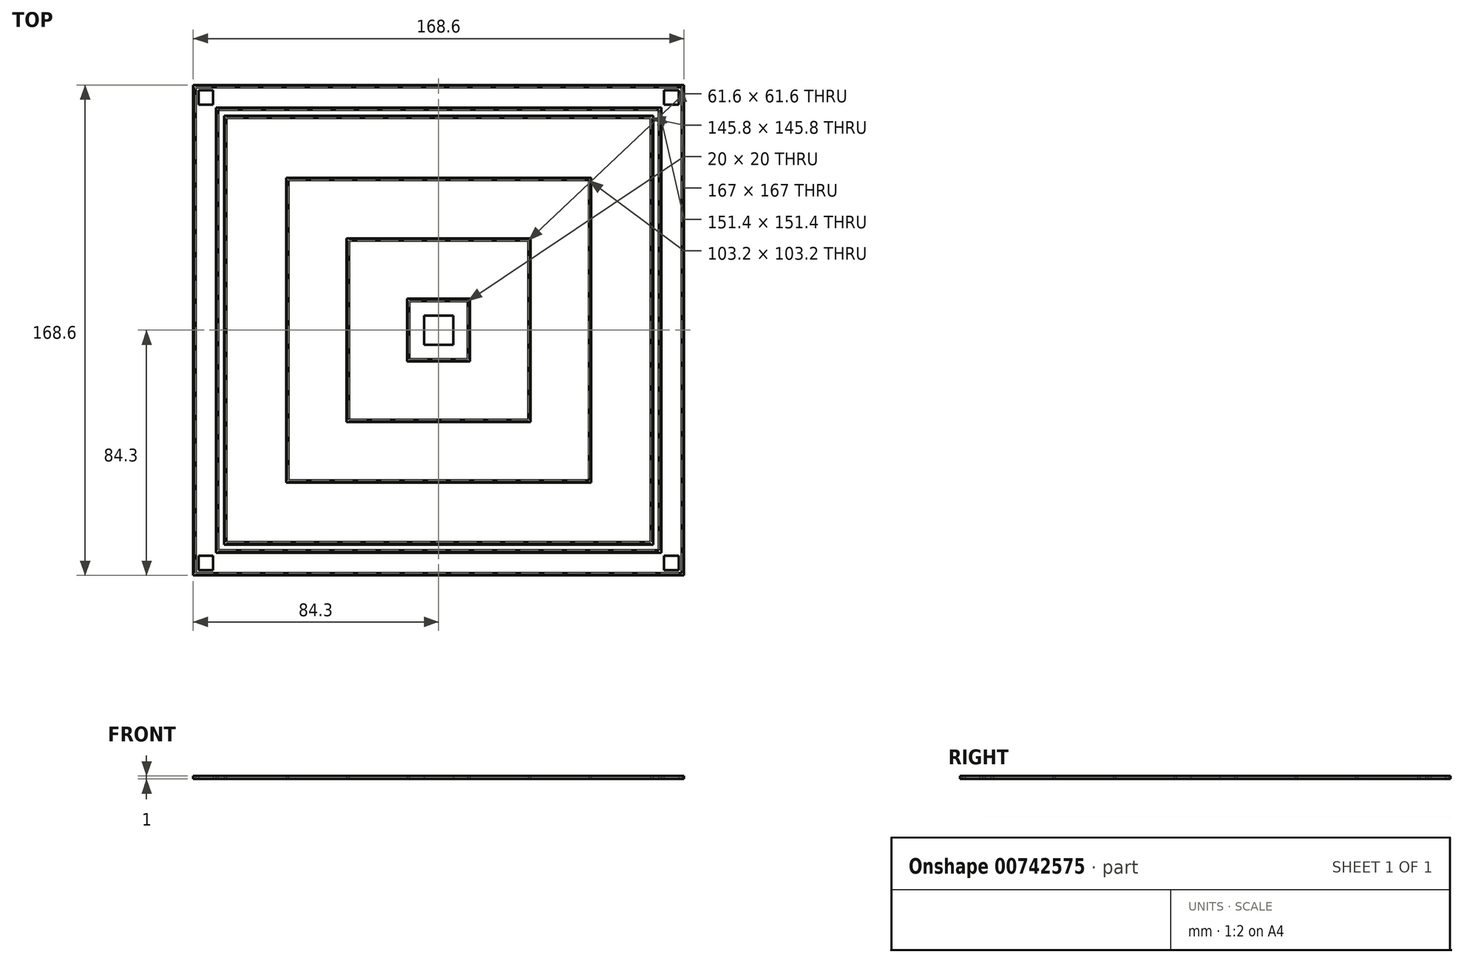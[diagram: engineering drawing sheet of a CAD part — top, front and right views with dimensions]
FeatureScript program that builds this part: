
annotation { "Feature Type Name" : "Feature", "Feature Type Description" : "" }
export const myFeature = defineFeature(function(context is Context, id is Id, definition is map)
    precondition{}
    {
        {
            var Q0;
            Q0=qCreatedBy(makeId("Top.planeOp"),FACE);
            var sketch = newSketch(context, id + "F0", { "sketchPlane" : qUnion([Q0])});
            skLineSegment(sketch, "E0.bottom", {"start": v(-80, 80) * mm, "end": v(80, 80) * mm, "construction": true});
            skLineSegment(sketch, "E0.top", {"start": v(-80, -80) * mm, "end": v(80, -80) * mm, "construction": true});
            skLineSegment(sketch, "E0.left", {"start": v(-80, 80) * mm, "end": v(-80, -80) * mm, "construction": true});
            skLineSegment(sketch, "E0.right", {"start": v(80, 80) * mm, "end": v(80, -80) * mm, "construction": true});
            skPoint(sketch, "E0.middle", {"position": v(0, 0) * mm});
            skLineSegment(sketch, "E1.bottom", {"start": v(-82.5, 82.5) * mm, "end": v(-77.5, 82.5) * mm});
            skLineSegment(sketch, "E1.top", {"start": v(-82.5, 77.5) * mm, "end": v(-77.5, 77.5) * mm});
            skLineSegment(sketch, "E1.left", {"start": v(-82.5, 82.5) * mm, "end": v(-82.5, 77.5) * mm});
            skLineSegment(sketch, "E1.right", {"start": v(-77.5, 82.5) * mm, "end": v(-77.5, 77.5) * mm});
            skPoint(sketch, "E1.middle", {"position": v(-80, 80) * mm});
            skLineSegment(sketch, "E2.bottom", {"start": v(-82.5, -77.5) * mm, "end": v(-77.5, -77.5) * mm});
            skLineSegment(sketch, "E2.top", {"start": v(-82.5, -82.5) * mm, "end": v(-77.5, -82.5) * mm});
            skLineSegment(sketch, "E2.left", {"start": v(-82.5, -77.5) * mm, "end": v(-82.5, -82.5) * mm});
            skLineSegment(sketch, "E2.right", {"start": v(-77.5, -77.5) * mm, "end": v(-77.5, -82.5) * mm});
            skPoint(sketch, "E2.middle", {"position": v(-80, -80) * mm});
            skLineSegment(sketch, "E3.bottom", {"start": v(77.5, -77.5) * mm, "end": v(82.5, -77.5) * mm});
            skLineSegment(sketch, "E3.top", {"start": v(77.5, -82.5) * mm, "end": v(82.5, -82.5) * mm});
            skLineSegment(sketch, "E3.left", {"start": v(77.5, -77.5) * mm, "end": v(77.5, -82.5) * mm});
            skLineSegment(sketch, "E3.right", {"start": v(82.5, -77.5) * mm, "end": v(82.5, -82.5) * mm});
            skPoint(sketch, "E3.middle", {"position": v(80, -80) * mm});
            skLineSegment(sketch, "E4.bottom", {"start": v(77.5, 77.5) * mm, "end": v(82.5, 77.5) * mm});
            skLineSegment(sketch, "E4.top", {"start": v(77.5, 82.5) * mm, "end": v(82.5, 82.5) * mm});
            skLineSegment(sketch, "E4.left", {"start": v(77.5, 77.5) * mm, "end": v(77.5, 82.5) * mm});
            skLineSegment(sketch, "E4.right", {"start": v(82.5, 77.5) * mm, "end": v(82.5, 82.5) * mm});
            skPoint(sketch, "E4.middle", {"position": v(80, 80) * mm});
            skLineSegment(sketch, "E5.bottom", {"start": v(-5, 5) * mm, "end": v(5, 5) * mm});
            skLineSegment(sketch, "E5.top", {"start": v(-5, -5) * mm, "end": v(5, -5) * mm});
            skLineSegment(sketch, "E5.left", {"start": v(-5, 5) * mm, "end": v(-5, -5) * mm});
            skLineSegment(sketch, "E5.right", {"start": v(5, 5) * mm, "end": v(5, -5) * mm});
            skLineSegment(sketch, "E6.bottom", {"start": v(-76.5, 76.5) * mm, "end": v(76.5, 76.5) * mm});
            skLineSegment(sketch, "E6.top", {"start": v(-76.5, -76.5) * mm, "end": v(76.5, -76.5) * mm});
            skLineSegment(sketch, "E6.left", {"start": v(-76.5, 76.5) * mm, "end": v(-76.5, -76.5) * mm});
            skLineSegment(sketch, "E6.right", {"start": v(76.5, 76.5) * mm, "end": v(76.5, -76.5) * mm});
            skLineSegment(sketch, "E7.bottom", {"start": v(-75.7, 75.7) * mm, "end": v(75.7, 75.7) * mm});
            skLineSegment(sketch, "E7.top", {"start": v(-75.7, -75.7) * mm, "end": v(75.7, -75.7) * mm});
            skLineSegment(sketch, "E7.left", {"start": v(-75.7, 75.7) * mm, "end": v(-75.7, -75.7) * mm});
            skLineSegment(sketch, "E7.right", {"start": v(75.7, 75.7) * mm, "end": v(75.7, -75.7) * mm});
            skLineSegment(sketch, "E8.bottom", {"start": v(-73.7, 73.7) * mm, "end": v(73.7, 73.7) * mm});
            skLineSegment(sketch, "E8.top", {"start": v(-73.7, -73.7) * mm, "end": v(73.7, -73.7) * mm});
            skLineSegment(sketch, "E8.left", {"start": v(-73.7, 73.7) * mm, "end": v(-73.7, -73.7) * mm});
            skLineSegment(sketch, "E8.right", {"start": v(73.7, 73.7) * mm, "end": v(73.7, -73.7) * mm});
            skLineSegment(sketch, "E9.bottom", {"start": v(-72.9, 72.9) * mm, "end": v(72.9, 72.9) * mm});
            skLineSegment(sketch, "E9.top", {"start": v(-72.9, -72.9) * mm, "end": v(72.9, -72.9) * mm});
            skLineSegment(sketch, "E9.left", {"start": v(-72.9, 72.9) * mm, "end": v(-72.9, -72.9) * mm});
            skLineSegment(sketch, "E9.right", {"start": v(72.9, 72.9) * mm, "end": v(72.9, -72.9) * mm});
            skLineSegment(sketch, "E10.bottom", {"start": v(-83.5, 83.5) * mm, "end": v(83.5, 83.5) * mm});
            skLineSegment(sketch, "E10.top", {"start": v(-83.5, -83.5) * mm, "end": v(83.5, -83.5) * mm});
            skLineSegment(sketch, "E10.left", {"start": v(-83.5, 83.5) * mm, "end": v(-83.5, -83.5) * mm});
            skLineSegment(sketch, "E10.right", {"start": v(83.5, 83.5) * mm, "end": v(83.5, -83.5) * mm});
            skLineSegment(sketch, "E11.bottom", {"start": v(-84.3, 84.3) * mm, "end": v(84.3, 84.3) * mm});
            skLineSegment(sketch, "E11.top", {"start": v(-84.3, -84.3) * mm, "end": v(84.3, -84.3) * mm});
            skLineSegment(sketch, "E11.left", {"start": v(-84.3, 84.3) * mm, "end": v(-84.3, -84.3) * mm});
            skLineSegment(sketch, "E11.right", {"start": v(84.3, 84.3) * mm, "end": v(84.3, -84.3) * mm});
            skLineSegment(sketch, "E12.bottom", {"start": v(-52.4, 52.4) * mm, "end": v(52.4, 52.4) * mm});
            skLineSegment(sketch, "E12.top", {"start": v(-52.4, -52.4) * mm, "end": v(52.4, -52.4) * mm});
            skLineSegment(sketch, "E12.left", {"start": v(-52.4, 52.4) * mm, "end": v(-52.4, -52.4) * mm});
            skLineSegment(sketch, "E12.right", {"start": v(52.4, 52.4) * mm, "end": v(52.4, -52.4) * mm});
            skLineSegment(sketch, "E13.bottom", {"start": v(-51.6, 51.6) * mm, "end": v(51.6, 51.6) * mm});
            skLineSegment(sketch, "E13.top", {"start": v(-51.6, -51.6) * mm, "end": v(51.6, -51.6) * mm});
            skLineSegment(sketch, "E13.left", {"start": v(-51.6, 51.6) * mm, "end": v(-51.6, -51.6) * mm});
            skLineSegment(sketch, "E13.right", {"start": v(51.6, 51.6) * mm, "end": v(51.6, -51.6) * mm});
            skLineSegment(sketch, "E14.bottom", {"start": v(-31.6, 31.6) * mm, "end": v(31.6, 31.6) * mm});
            skLineSegment(sketch, "E14.top", {"start": v(-31.6, -31.6) * mm, "end": v(31.6, -31.6) * mm});
            skLineSegment(sketch, "E14.left", {"start": v(-31.6, 31.6) * mm, "end": v(-31.6, -31.6) * mm});
            skLineSegment(sketch, "E14.right", {"start": v(31.6, 31.6) * mm, "end": v(31.6, -31.6) * mm});
            skLineSegment(sketch, "E15.bottom", {"start": v(-30.8, 30.8) * mm, "end": v(30.8, 30.8) * mm});
            skLineSegment(sketch, "E15.top", {"start": v(-30.8, -30.8) * mm, "end": v(30.8, -30.8) * mm});
            skLineSegment(sketch, "E15.left", {"start": v(-30.8, 30.8) * mm, "end": v(-30.8, -30.8) * mm});
            skLineSegment(sketch, "E15.right", {"start": v(30.8, 30.8) * mm, "end": v(30.8, -30.8) * mm});
            skLineSegment(sketch, "E16.bottom", {"start": v(-10.8, 10.8) * mm, "end": v(10.8, 10.8) * mm});
            skLineSegment(sketch, "E16.top", {"start": v(-10.8, -10.8) * mm, "end": v(10.8, -10.8) * mm});
            skLineSegment(sketch, "E16.left", {"start": v(-10.8, 10.8) * mm, "end": v(-10.8, -10.8) * mm});
            skLineSegment(sketch, "E16.right", {"start": v(10.8, 10.8) * mm, "end": v(10.8, -10.8) * mm});
            skLineSegment(sketch, "E17.bottom", {"start": v(-10, 10) * mm, "end": v(10, 10) * mm});
            skLineSegment(sketch, "E17.top", {"start": v(-10, -10) * mm, "end": v(10, -10) * mm});
            skLineSegment(sketch, "E17.left", {"start": v(-10, 10) * mm, "end": v(-10, -10) * mm});
            skLineSegment(sketch, "E17.right", {"start": v(10, 10) * mm, "end": v(10, -10) * mm});
            skLineSegment(sketch, "E18.top", {"start": v(-80, -80) * mm, "end": v(80, -80) * mm});
            skSolve(sketch);
        }
        {
            var Q0;
            Q0=makeQuery(id+"F0.imprint","IMPRINT",FACE,{"disambiguationData":[TD([[makeQuery(id+"F0.imprint","IMPRINT",EDGE,{"derivedFrom":sQuery(id+"F0.wireOp",EDGE,"E10.bottom")}),1.0]])]});
            var Q1;
            {var subQ1=sQuery(id+"F0.wireOp",EDGE,"E1.bottom");Q1=makeQuery(id+"F0.imprint","IMPRINT",FACE,{"disambiguationData":[TD([[makeQuery(id+"F0.imprint","IMPRINT",EDGE,{"derivedFrom":subQ1}),-1.0]])]});}
            var Q2;
            {var subQ3=sQuery(id+"F0.wireOp",EDGE,"E18.left");var subQ5=sQuery(id+"F0.wireOp",EDGE,"E18.bottom");var subQ7=makeQuery(id+"F0.imprint","INTERSECT",VERTEX,{"derivedFrom":[subQ5,subQ3]});Q2=makeQuery(id+"F0.imprint","IMPRINT",FACE,{"disambiguationData":[TD([[makeQuery(id+"F0.imprint","IMPRINT",EDGE,{"disambiguationData":[TD([[subQ7,-1.0]])],"derivedFrom":subQ5}),-1.0]])]});}
            var Q3;
            {var subQ0=sQuery(id+"F0.wireOp",EDGE,"qftvMAqE-KtSR-YpLS-TIVa-jHuJledwcVvA.left");Q3=makeQuery(id+"F0.imprint","IMPRINT",FACE,{"disambiguationData":[TD([[makeQuery(id+"F0.imprint","IMPRINT",EDGE,{"derivedFrom":subQ0}),-1.0]])]});}
            var Q4;
            {var subQ0=sQuery(id+"F0.wireOp",EDGE,"qftvMAqE-KtSR-YpLS-TIVa-jHuJledwcVvA.bottom");Q4=makeQuery(id+"F0.imprint","IMPRINT",FACE,{"disambiguationData":[TD([[makeQuery(id+"F0.imprint","IMPRINT",EDGE,{"derivedFrom":subQ0}),1.0]])]});}
            var Q5;
            Q5=makeQuery(id+"F0.imprint","IMPRINT",FACE,{"disambiguationData":[TD([[makeQuery(id+"F0.imprint","IMPRINT",EDGE,{"derivedFrom":sQuery(id+"F0.wireOp",EDGE,"E6.bottom")}),-1.0]])]});
            var Q6;
            Q6=makeQuery(id+"F0.imprint","IMPRINT",FACE,{"disambiguationData":[TD([[makeQuery(id+"F0.imprint","IMPRINT",EDGE,{"derivedFrom":sQuery(id+"F0.wireOp",EDGE,"E8.bottom")}),-1.0]])]});
            var Q7;
            Q7=makeQuery(id+"F0.imprint","IMPRINT",FACE,{"disambiguationData":[TD([[makeQuery(id+"F0.imprint","IMPRINT",EDGE,{"derivedFrom":sQuery(id+"F0.wireOp",EDGE,"E12.bottom")}),-1.0]])]});
            var Q8;
            Q8=makeQuery(id+"F0.imprint","IMPRINT",FACE,{"disambiguationData":[TD([[makeQuery(id+"F0.imprint","IMPRINT",EDGE,{"derivedFrom":sQuery(id+"F0.wireOp",EDGE,"E14.bottom")}),-1.0]])]});
            var Q9;
            Q9=makeQuery(id+"F0.imprint","IMPRINT",FACE,{"disambiguationData":[TD([[makeQuery(id+"F0.imprint","IMPRINT",EDGE,{"derivedFrom":sQuery(id+"F0.wireOp",EDGE,"E16.bottom")}),-1.0]])]});
            var Q10;
            Q10=makeQuery(id+"F0.imprint","IMPRINT",FACE,{"disambiguationData":[TD([[makeQuery(id+"F0.imprint","IMPRINT",EDGE,{"derivedFrom":sQuery(id+"F0.wireOp",EDGE,"E5.bottom")}),-1.0]])]});
            var Q11;
            {var subQ3=sQuery(id+"F0.wireOp",EDGE,"E18.right");var subQ5=sQuery(id+"F0.wireOp",EDGE,"E18.bottom");var subQ7=makeQuery(id+"F0.imprint","INTERSECT",VERTEX,{"derivedFrom":[subQ5,subQ3]});Q11=makeQuery(id+"F0.imprint","IMPRINT",FACE,{"disambiguationData":[TD([[makeQuery(id+"F0.imprint","IMPRINT",EDGE,{"disambiguationData":[TD([[subQ7,1.0]])],"derivedFrom":subQ5}),-1.0]])]});}
            var Q12;
            {var subQ7=sQuery(id+"F0.wireOp",EDGE,"E4.top");Q12=makeQuery(id+"F0.imprint","IMPRINT",FACE,{"disambiguationData":[TD([[makeQuery(id+"F0.imprint","IMPRINT",EDGE,{"derivedFrom":subQ7}),-1.0]])]});}
            var Q13;
            {var subQ0=sQuery(id+"F0.wireOp",EDGE,"qftvMAqE-KtSR-YpLS-TIVa-jHuJledwcVvA.right");Q13=makeQuery(id+"F0.imprint","IMPRINT",FACE,{"disambiguationData":[TD([[makeQuery(id+"F0.imprint","IMPRINT",EDGE,{"derivedFrom":subQ0}),1.0]])]});}
            var Q14;
            {var subQ2=sQuery(id+"F0.wireOp",EDGE,"E3.top");Q14=makeQuery(id+"F0.imprint","IMPRINT",FACE,{"disambiguationData":[TD([[makeQuery(id+"F0.imprint","IMPRINT",EDGE,{"derivedFrom":subQ2}),1.0]])]});}
            var Q15;
            {var subQ3=sQuery(id+"F0.wireOp",EDGE,"E18.right");var subQ5=sQuery(id+"F0.wireOp",EDGE,"E18.top");var subQ7=makeQuery(id+"F0.imprint","INTERSECT",VERTEX,{"derivedFrom":[subQ5,subQ3]});Q15=makeQuery(id+"F0.imprint","IMPRINT",FACE,{"disambiguationData":[TD([[makeQuery(id+"F0.imprint","IMPRINT",EDGE,{"disambiguationData":[TD([[subQ7,1.0]])],"derivedFrom":subQ5}),1.0]])]});}
            var Q16;
            {var subQ0=sQuery(id+"F0.wireOp",EDGE,"qftvMAqE-KtSR-YpLS-TIVa-jHuJledwcVvA.top");Q16=makeQuery(id+"F0.imprint","IMPRINT",FACE,{"disambiguationData":[TD([[makeQuery(id+"F0.imprint","IMPRINT",EDGE,{"derivedFrom":subQ0}),-1.0]])]});}
            var Q17;
            {var subQ1=sQuery(id+"F0.wireOp",EDGE,"E2.top");Q17=makeQuery(id+"F0.imprint","IMPRINT",FACE,{"disambiguationData":[TD([[makeQuery(id+"F0.imprint","IMPRINT",EDGE,{"derivedFrom":subQ1}),1.0]])]});}
            var Q18;
            {var subQ3=sQuery(id+"F0.wireOp",EDGE,"E18.left");var subQ5=sQuery(id+"F0.wireOp",EDGE,"E18.top");var subQ7=makeQuery(id+"F0.imprint","INTERSECT",VERTEX,{"derivedFrom":[subQ5,subQ3]});Q18=makeQuery(id+"F0.imprint","IMPRINT",FACE,{"disambiguationData":[TD([[makeQuery(id+"F0.imprint","IMPRINT",EDGE,{"disambiguationData":[TD([[subQ7,-1.0]])],"derivedFrom":subQ5}),1.0]])]});}
            extrude(context, id + "F1", {"entities" : qUnion([Q0, Q1, Q2, Q3, Q4, Q5, Q6, Q7, Q8, Q9, Q10, Q11, Q12, Q13, Q14, Q15, Q16, Q17, Q18]), "depth" : 1 * mm, "offsetDistance" : 25 * mm});
        }
    });
